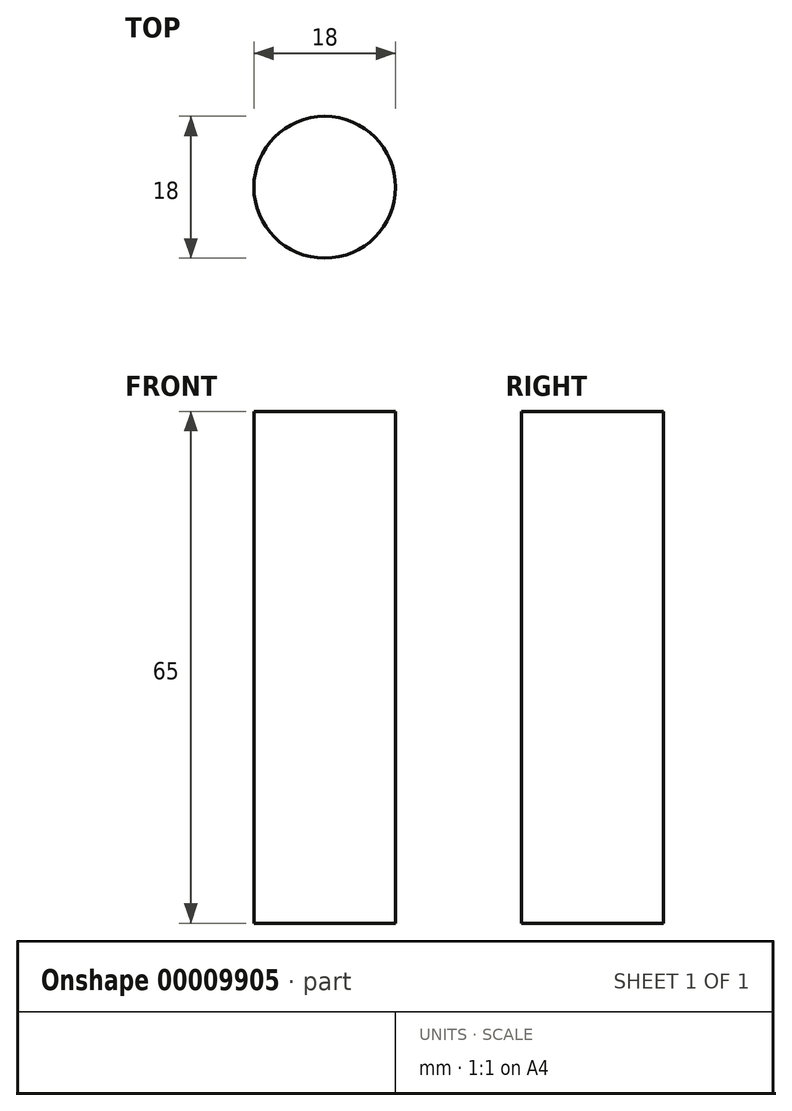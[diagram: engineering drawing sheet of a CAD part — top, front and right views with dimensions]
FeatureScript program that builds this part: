
annotation { "Feature Type Name" : "Feature", "Feature Type Description" : "" }
export const myFeature = defineFeature(function(context is Context, id is Id, definition is map)
    precondition{}
    {
        {
            var Q0;
            Q0=qCreatedBy(makeId("Top.planeOp"),FACE);
            var sketch = newSketch(context, id + "F0", { "sketchPlane" : qUnion([Q0])});
            skCircle(sketch, "E0", {"center": v(0, 0) * mm, "radius": 9 * mm});
            skSolve(sketch);
        }
        {
            var Q0;
            Q0 = qSketchRegion(id + "F0", true);
            extrude(context, id + "F1", {"entities" : qUnion([Q0]), "depth" : 65 * mm});
        }
    });
